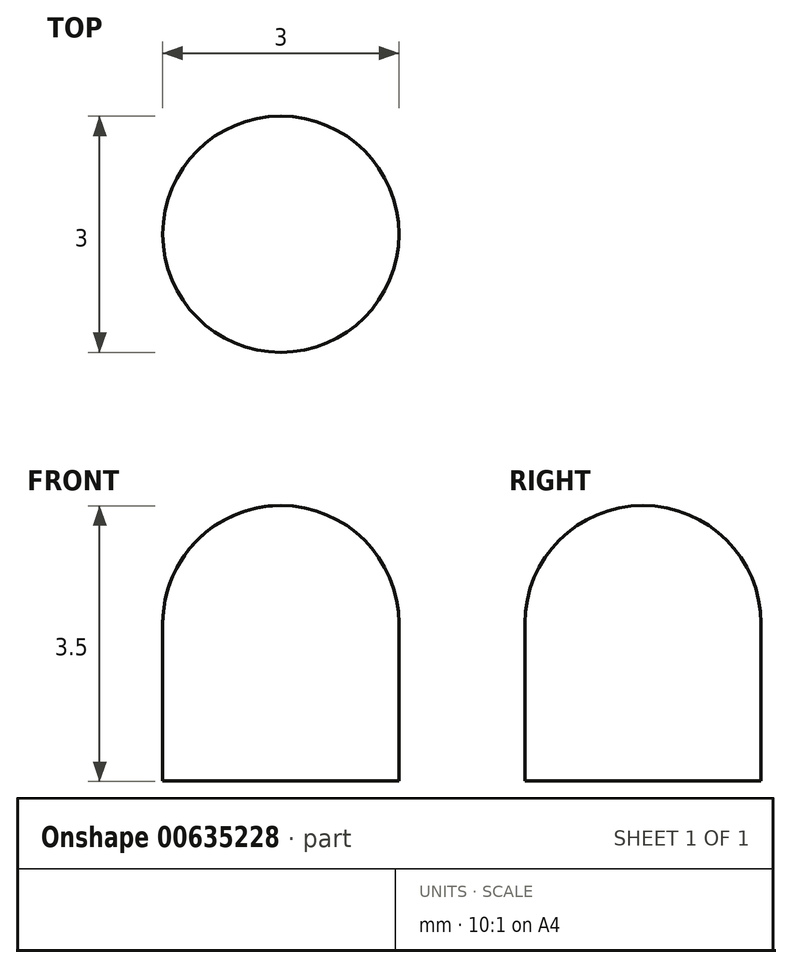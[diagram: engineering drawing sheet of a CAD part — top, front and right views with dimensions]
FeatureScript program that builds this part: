
annotation { "Feature Type Name" : "Feature", "Feature Type Description" : "" }
export const myFeature = defineFeature(function(context is Context, id is Id, definition is map)
    precondition{}
    {
        {
            var Q0;
            Q0=qCreatedBy(makeId("Front.planeOp"),FACE);
            var sketch = newSketch(context, id + "F0", { "sketchPlane" : qUnion([Q0])});
            skLineSegment(sketch, "E0", {"start": v(0, 49.28) * mm, "end": v(0, -52.68) * mm, "construction": true});
            skLineSegment(sketch, "E1", {"start": v(-1.5, -1.15) * mm, "end": v(-1.5, 0.85) * mm});
            skArc(sketch, "E2", {"start": v(0, 2.35) * mm, "mid": v(-1.06, 1.91) * mm, "end": v(-1.5, 0.85) * mm});
            skLineSegment(sketch, "E3", {"start": v(-1.5, -1.15) * mm, "end": v(0, -1.15) * mm});
            skLineSegment(sketch, "E4", {"start": v(0, -1.15) * mm, "end": v(0, 2.35) * mm});
            skSolve(sketch);
        }
        {
            var Q0;
            Q0=qSketchRegion(id+"F0",true);
            var Q1;
            Q1=sQuery(id+"F0.wireOp",EDGE,"E0");
            revolve(context, id + "F1", {"entities" : qUnion([Q0]), "axis" : qUnion([Q1]), "revolveType" : RevolveType.FULL});
        }
    });
